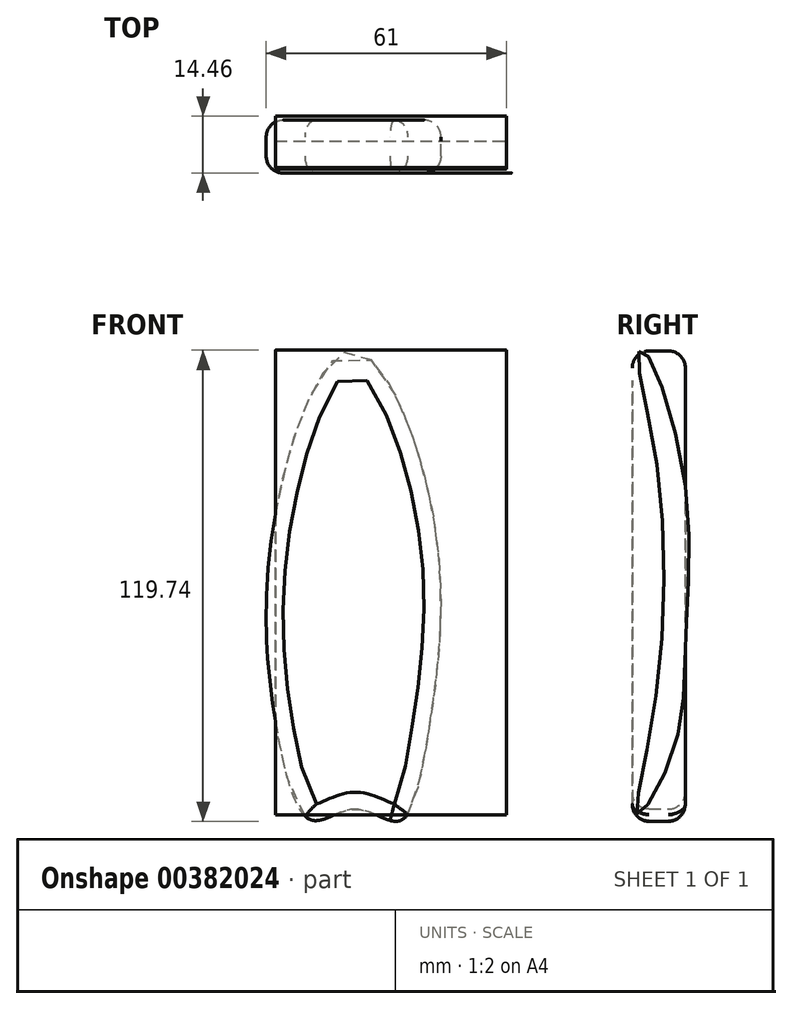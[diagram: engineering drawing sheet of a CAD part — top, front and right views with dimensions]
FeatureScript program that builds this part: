
annotation { "Feature Type Name" : "Feature", "Feature Type Description" : "" }
export const myFeature = defineFeature(function(context is Context, id is Id, definition is map)
    precondition{}
    {
        {
            var Q0;
            Q0=qCreatedBy(makeId("Front.planeOp"),FACE);
            var sketch = newSketch(context, id + "F0", { "sketchPlane" : qUnion([Q0])});
            skFitSpline(sketch, "E0", {"points": [v(-39.23, 42.98) * mm, v(-18.37, 0) * mm, v(-20.27, -56.74) * mm, v(-27.28, -76.46) * mm, v(-38.28, -73.43) * mm, v(-49.28, -76.27) * mm, v(-57.8, -55.99) * mm, v(-58.95, 0) * mm, v(-39.23, 42.98) * mm]});
            skSolve(sketch);
        }
        {
            var Q0;
            Q0 = qSketchRegion(id + "F0", true);
            extrude(context, id + "F1", {"entities" : qUnion([Q0]), "depth" : 13.46 * mm});
        }
        {
            var Q0;
            Q0=makeQuery(id+"F1.opExtrude","SWEPT_FACE",FACE,{"disambiguationData":[OSD([sQuery(id+"F0.wireOp",EDGE,"E0")])]});
            fillet(context, id + "F2", {"entities" : qUnion([Q0]), "radius" : 4.3 * mm, "tangentPropagation" : true, "allowEdgeOverflow" : false});
        }
        {
            var Q0;
            Q0=qCreatedBy(makeId("Right.planeOp"),FACE);
            var sketch = newSketch(context, id + "F3", { "sketchPlane" : qUnion([Q0])});
            skFitSpline(sketch, "E1", {"points": [v(-11.78, 42.77) * mm, v(-7.33, 14.76) * mm, v(-8.4, -51.35) * mm, v(-11.97, -74.86) * mm, v(-3.03, -58.6) * mm, v(0, -31.03) * mm, v(0, 8.6) * mm, v(-10.26, 42.77) * mm, v(-11.78, 42.77) * mm]});
            skSolve(sketch);
        }
        {
            var Q0;
            Q0=makeQuery(id+"F3.imprint","IMPRINT",FACE,{"disambiguationData":[TD([[makeQuery(id+"F3.imprint","IMPRINT",EDGE,{"derivedFrom":sQuery(id+"F3.wireOp",EDGE,"E1")}),1.0]])]});
            extrude(context, id + "F4", {"entities" : qUnion([Q0]), "oppositeDirection" : true, "depth" : 58.67 * mm});
        }
    });
